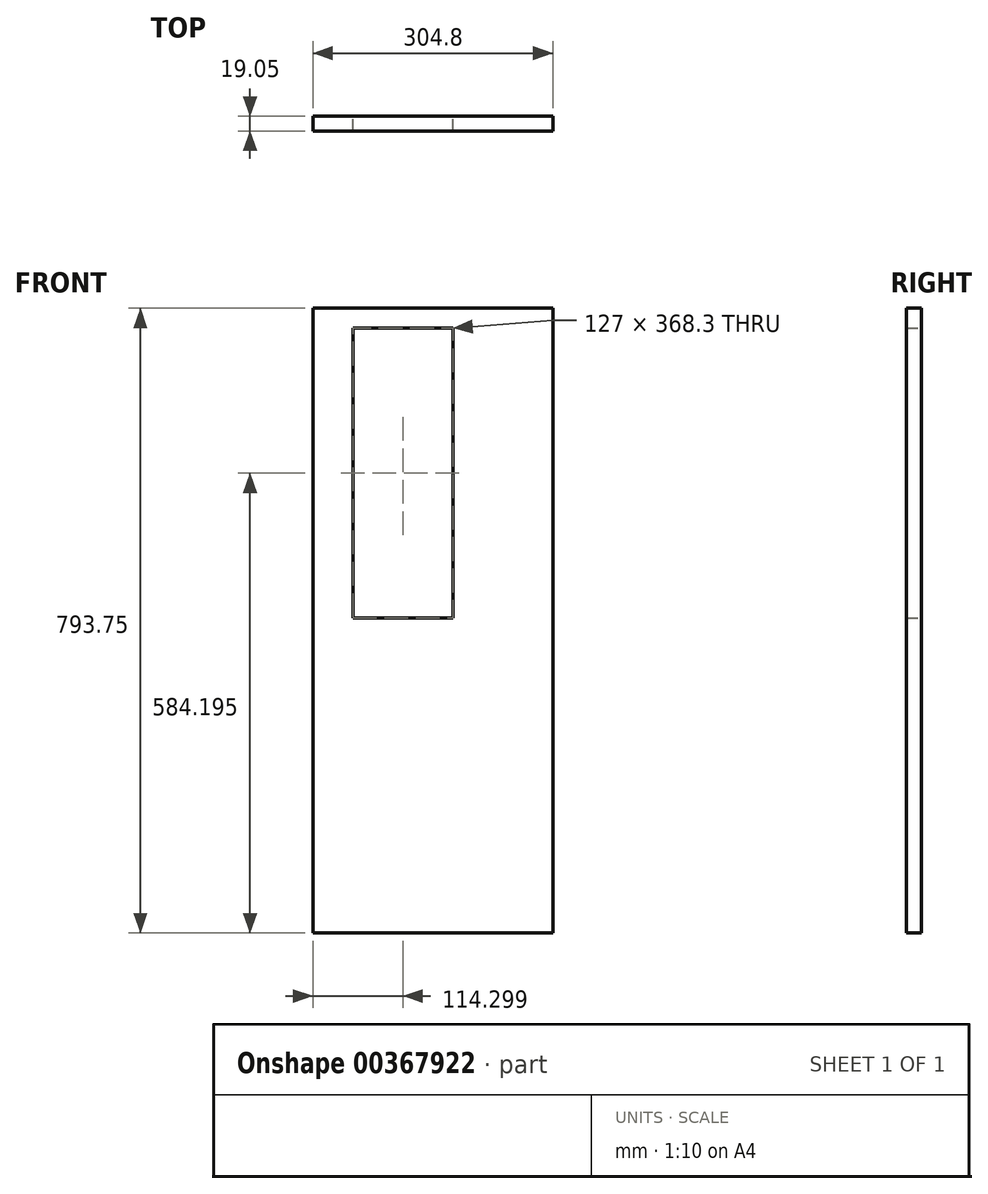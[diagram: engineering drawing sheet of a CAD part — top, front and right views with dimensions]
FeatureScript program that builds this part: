
annotation { "Feature Type Name" : "Feature", "Feature Type Description" : "" }
export const myFeature = defineFeature(function(context is Context, id is Id, definition is map)
    precondition{}
    {
        {
            var Q0;
            Q0=qCreatedBy(makeId("Front.planeOp"),FACE);
            var sketch = newSketch(context, id + "F0", { "sketchPlane" : qUnion([Q0])});
            skLineSegment(sketch, "E0.bottom", {"start": v(-171.66, 569.58) * mm, "end": v(133.14, 569.58) * mm});
            skLineSegment(sketch, "E0.top", {"start": v(-171.66, -224.17) * mm, "end": v(133.14, -224.17) * mm});
            skLineSegment(sketch, "E0.left", {"start": v(-171.66, 569.58) * mm, "end": v(-171.66, -224.17) * mm});
            skLineSegment(sketch, "E0.right", {"start": v(133.14, 569.58) * mm, "end": v(133.14, -224.17) * mm});
            skLineSegment(sketch, "E1.bottom", {"start": v(-120.86, 544.18) * mm, "end": v(6.14, 544.18) * mm});
            skLineSegment(sketch, "E1.top", {"start": v(-120.86, 175.88) * mm, "end": v(6.14, 175.88) * mm});
            skLineSegment(sketch, "E1.left", {"start": v(-120.86, 544.18) * mm, "end": v(-120.86, 175.88) * mm});
            skLineSegment(sketch, "E1.right", {"start": v(6.14, 544.18) * mm, "end": v(6.14, 175.88) * mm});
            skSolve(sketch);
        }
        {
            var Q0;
            Q0=makeQuery(id+"F0.imprint","IMPRINT",FACE,{"disambiguationData":[TD([[makeQuery(id+"F0.imprint","IMPRINT",EDGE,{"derivedFrom":sQuery(id+"F0.wireOp",EDGE,"E0.bottom")}),-1.0]])]});
            extrude(context, id + "F1", {"entities" : qUnion([Q0]), "depth" : 19.05 * mm});
        }
    });
